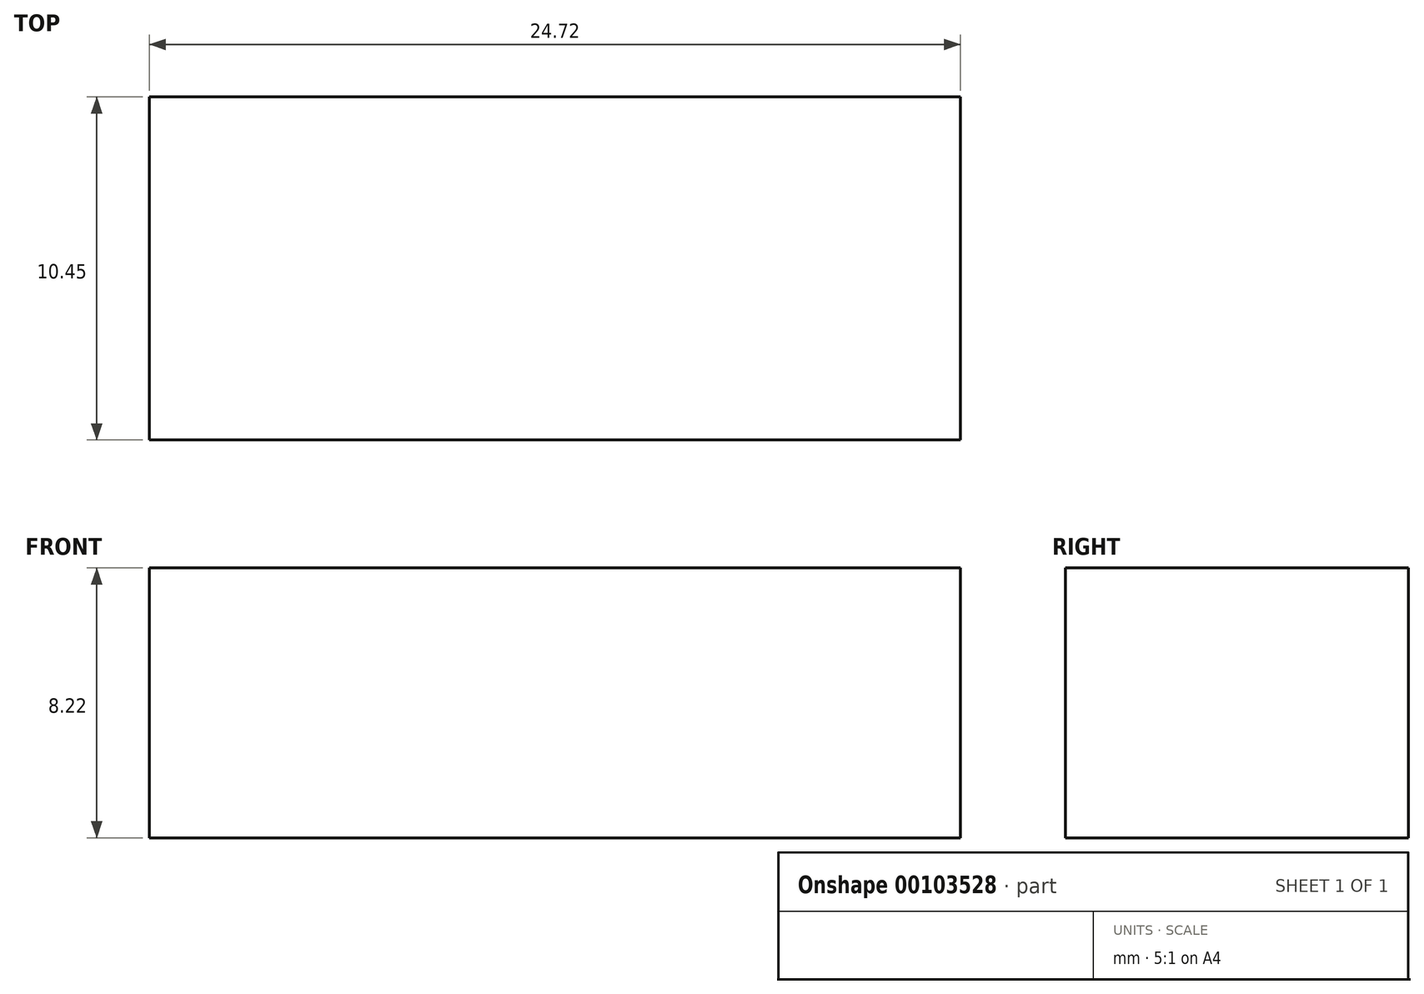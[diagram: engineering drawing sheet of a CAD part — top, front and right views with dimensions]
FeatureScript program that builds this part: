
annotation { "Feature Type Name" : "Feature", "Feature Type Description" : "" }
export const myFeature = defineFeature(function(context is Context, id is Id, definition is map)
    precondition{}
    {
        {
            var Q0;
            Q0=qCreatedBy(makeId("Top.planeOp"),FACE);
            var sketch = newSketch(context, id + "F0", { "sketchPlane" : qUnion([Q0])});
            skLineSegment(sketch, "E0.bottom", {"start": v(-5.19, 6.12) * mm, "end": v(19.53, 6.12) * mm});
            skLineSegment(sketch, "E0.top", {"start": v(-5.19, -4.33) * mm, "end": v(19.53, -4.33) * mm});
            skLineSegment(sketch, "E0.left", {"start": v(-5.19, 6.12) * mm, "end": v(-5.19, -4.33) * mm});
            skLineSegment(sketch, "E0.right", {"start": v(19.53, 6.12) * mm, "end": v(19.53, -4.33) * mm});
            skSolve(sketch);
        }
        {
            var Q0;
            Q0=makeQuery(id+"F0.imprint","IMPRINT",FACE,{"disambiguationData":[TD([[makeQuery(id+"F0.imprint","IMPRINT",EDGE,{"derivedFrom":sQuery(id+"F0.wireOp",EDGE,"E0.bottom")}),-1.0]])]});
            extrude(context, id + "F1", {"entities" : qUnion([Q0]), "depth" : 8.22 * mm});
        }
    });
